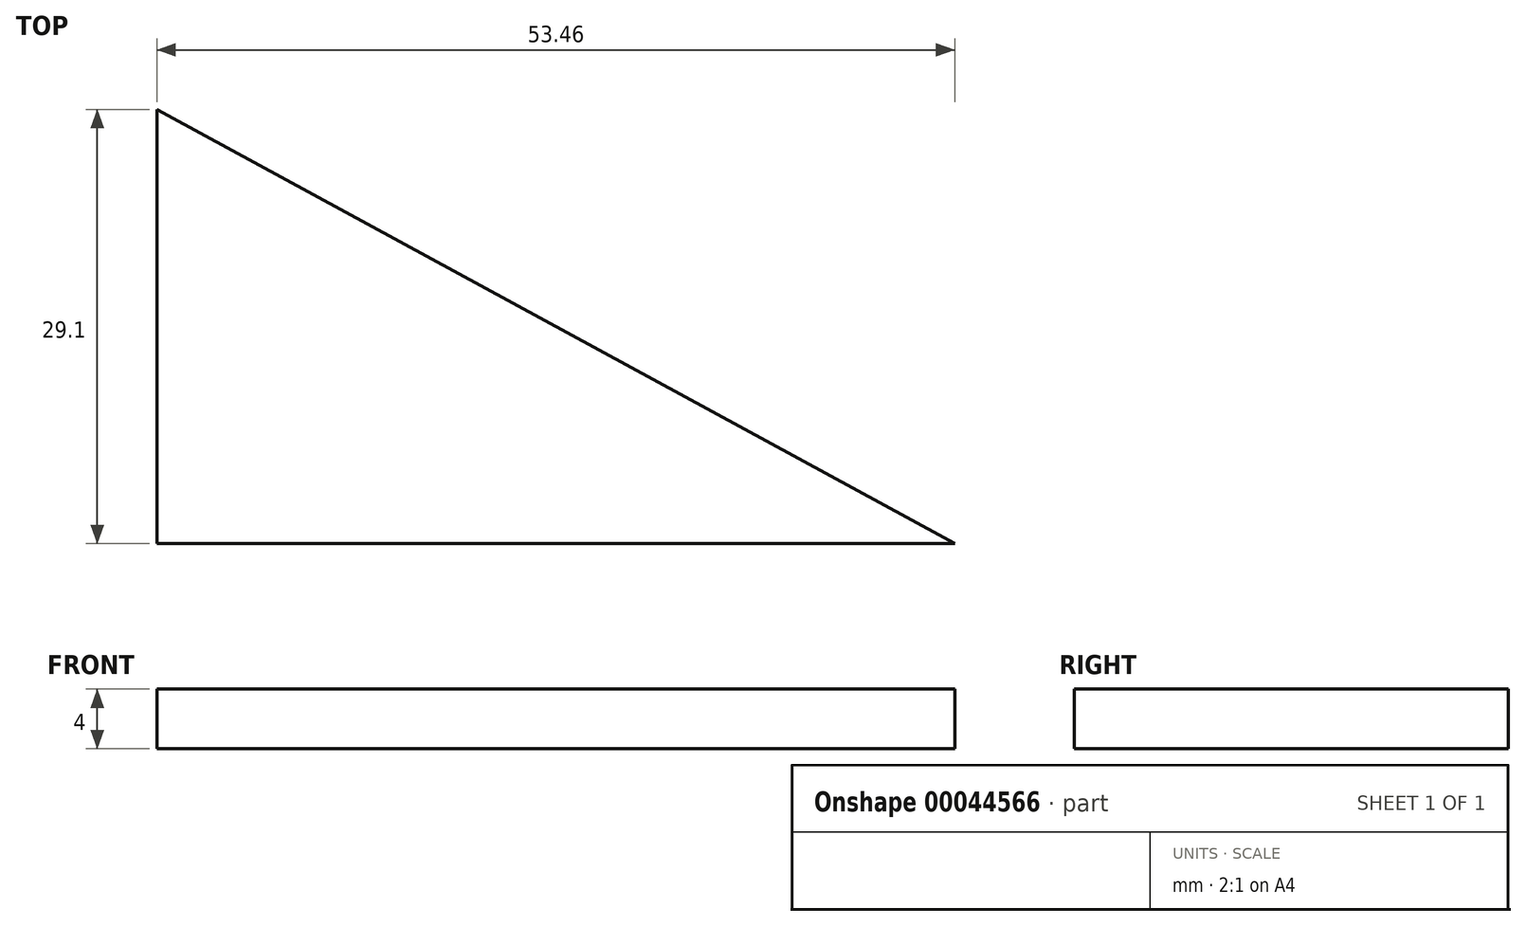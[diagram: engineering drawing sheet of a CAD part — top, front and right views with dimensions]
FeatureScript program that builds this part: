
annotation { "Feature Type Name" : "Feature", "Feature Type Description" : "" }
export const myFeature = defineFeature(function(context is Context, id is Id, definition is map)
    precondition{}
    {
        {
            var Q0;
            Q0=qCreatedBy(makeId("Top.planeOp"),FACE);
            var sketch = newSketch(context, id + "F0", { "sketchPlane" : qUnion([Q0])});
            skLineSegment(sketch, "E0.rect.top", {"start": v(-26.73, -14.55) * mm, "end": v(26.73, -14.55) * mm});
            skLineSegment(sketch, "E0.rect.left", {"start": v(-26.73, 14.55) * mm, "end": v(-26.73, -14.55) * mm});
            skPoint(sketch, "E0.rect.middle", {"position": v(0, 0) * mm});
            skLineSegment(sketch, "E1", {"start": v(-26.73, 14.55) * mm, "end": v(26.73, -14.55) * mm});
            skSolve(sketch);
        }
        {
            var Q0;
            Q0=makeQuery(id+"F0.imprint","IMPRINT",FACE,{"disambiguationData":[TD([[makeQuery(id+"F0.imprint","IMPRINT",EDGE,{"derivedFrom":sQuery(id+"F0.wireOp",EDGE,"E0.rect.top")}),1.0]])]});
            extrude(context, id + "F1", {"entities" : qUnion([Q0]), "depth" : 4 * mm});
        }
    });
